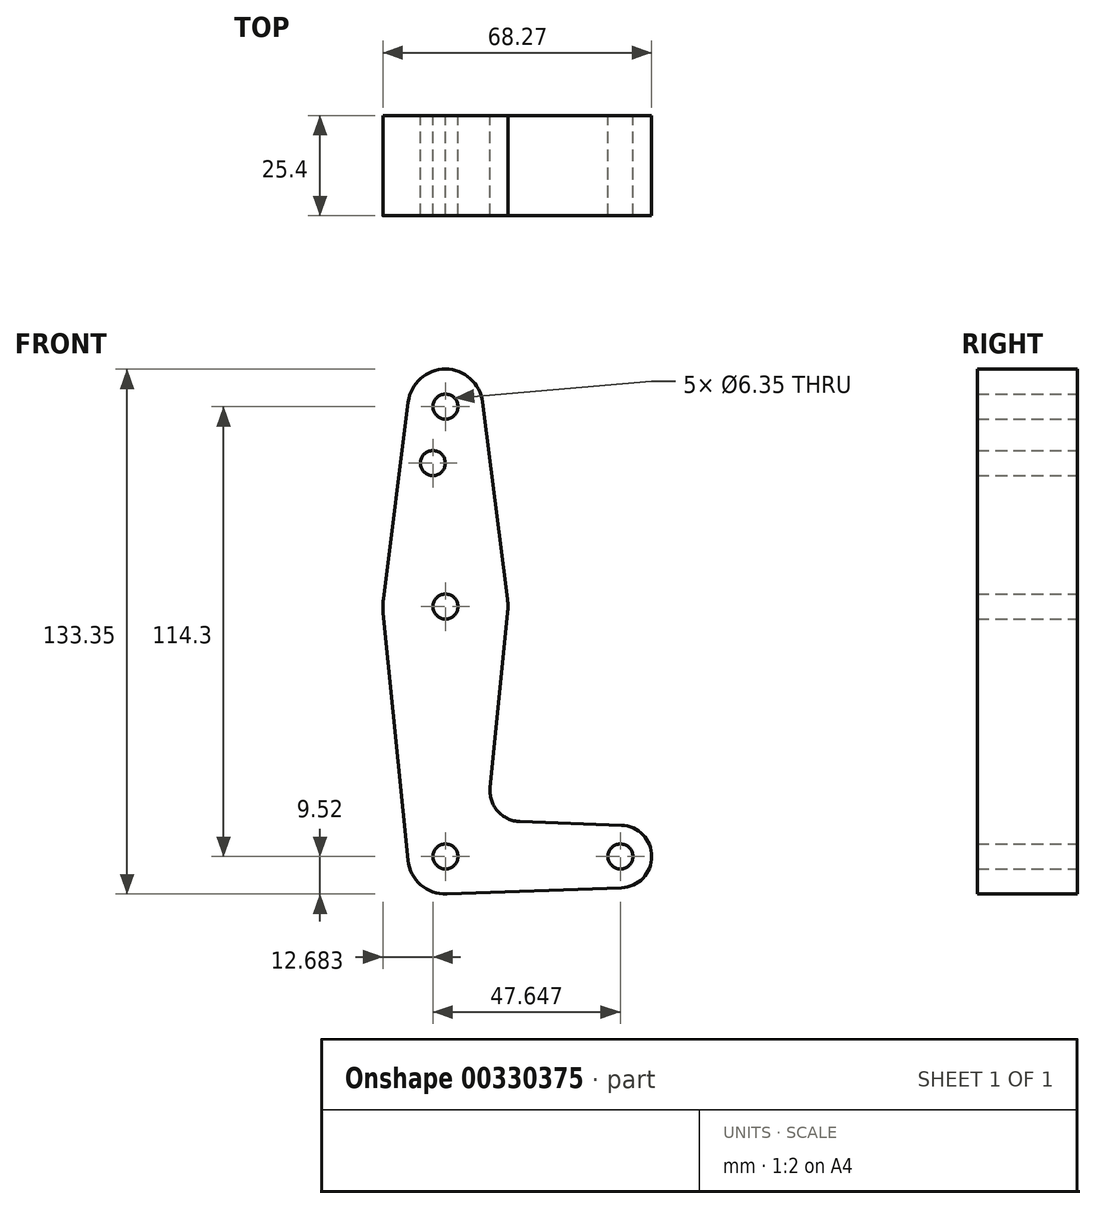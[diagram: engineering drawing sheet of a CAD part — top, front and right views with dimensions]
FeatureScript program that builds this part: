
annotation { "Feature Type Name" : "Feature", "Feature Type Description" : "" }
export const myFeature = defineFeature(function(context is Context, id is Id, definition is map)
    precondition{}
    {
        {
            var Q0;
            Q0=qCreatedBy(makeId("Front.planeOp"),FACE);
            var sketch = newSketch(context, id + "F0", { "sketchPlane" : qUnion([Q0])});
            skLineSegment(sketch, "E0", {"start": v(0, 114.3) * mm, "end": v(0, 0) * mm, "construction": true});
            skLineSegment(sketch, "E1", {"start": v(0, 0) * mm, "end": v(44.45, 0) * mm, "construction": true});
            skCircle(sketch, "E2", {"center": v(0, 114.3) * mm, "radius": 9.53 * mm});
            skCircle(sketch, "E3", {"center": v(0, 63.5) * mm, "radius": 15.88 * mm});
            skCircle(sketch, "E4", {"center": v(0, 0) * mm, "radius": 9.53 * mm});
            skCircle(sketch, "E5", {"center": v(44.45, 0) * mm, "radius": 7.94 * mm});
            skLineSegment(sketch, "E6", {"start": v(-9.45, 115.5) * mm, "end": v(-15.75, 65.48) * mm});
            skLineSegment(sketch, "E7", {"start": v(9.45, 115.5) * mm, "end": v(15.75, 65.48) * mm});
            skLineSegment(sketch, "E8", {"start": v(-15.8, 61.91) * mm, "end": v(-9.48, -0.95) * mm});
            skLineSegment(sketch, "E9", {"start": v(15.8, 61.91) * mm, "end": v(11.34, 17.6) * mm});
            skLineSegment(sketch, "E10", {"start": v(18.97, 8.85) * mm, "end": v(44.73, 7.93) * mm});
            skLineSegment(sketch, "E11", {"start": v(0.34, -9.52) * mm, "end": v(44.73, -7.93) * mm});
            skCircle(sketch, "E12", {"center": v(0, 114.3) * mm, "radius": 3.18 * mm});
            skCircle(sketch, "E13", {"center": v(0, 63.5) * mm, "radius": 3.18 * mm});
            skCircle(sketch, "E14", {"center": v(0, 0) * mm, "radius": 3.18 * mm});
            skCircle(sketch, "E15", {"center": v(44.45, 0) * mm, "radius": 3.18 * mm});
            skCircle(sketch, "E16", {"center": v(-3.2, 99.96) * mm, "radius": 3.18 * mm});
            skArc(sketch, "E17.filletArc", {"start": v(11.34, 17.6) * mm, "mid": v(13.26, 11.57) * mm, "end": v(18.97, 8.85) * mm});
            skSolve(sketch);
        }
        {
            var Q0;
            Q0 = qSketchRegion(id + "FVLpB69krv67lIz_0", true);
            var Q1;
            {var subQ0=sQuery(id+"F0.wireOp",EDGE,"E6");Q1=makeQuery(id+"F0.imprint","IMPRINT",FACE,{"disambiguationData":[TD([[makeQuery(id+"F0.imprint","IMPRINT",EDGE,{"derivedFrom":subQ0}),1.0]])]});}
            var Q2;
            {var subQ3=sQuery(id+"F0.wireOp",EDGE,"E8");Q2=makeQuery(id+"F0.imprint","IMPRINT",FACE,{"disambiguationData":[TD([[makeQuery(id+"F0.imprint","IMPRINT",EDGE,{"derivedFrom":subQ3}),1.0]])]});}
            var Q3;
            Q3=makeQuery(id+"F0.imprint","IMPRINT",FACE,{"disambiguationData":[TD([[makeQuery(id+"F0.imprint","IMPRINT",EDGE,{"derivedFrom":sQuery(id+"F0.wireOp",EDGE,"E12")}),-1.0]])]});
            var Q4;
            Q4=makeQuery(id+"F0.imprint","IMPRINT",FACE,{"disambiguationData":[TD([[makeQuery(id+"F0.imprint","IMPRINT",EDGE,{"derivedFrom":sQuery(id+"F0.wireOp",EDGE,"E13")}),-1.0]])]});
            var Q5;
            Q5=makeQuery(id+"F0.imprint","IMPRINT",FACE,{"disambiguationData":[TD([[makeQuery(id+"F0.imprint","IMPRINT",EDGE,{"derivedFrom":sQuery(id+"F0.wireOp",EDGE,"E14")}),-1.0]])]});
            var Q6;
            Q6=makeQuery(id+"F0.imprint","IMPRINT",FACE,{"disambiguationData":[TD([[makeQuery(id+"F0.imprint","IMPRINT",EDGE,{"derivedFrom":sQuery(id+"F0.wireOp",EDGE,"E15")}),-1.0]])]});
            extrude(context, id + "F1", {"entities" : qUnion([Q0, Q1, Q2, Q3, Q4, Q5, Q6]), "depth" : 25.4 * mm});
        }
    });
